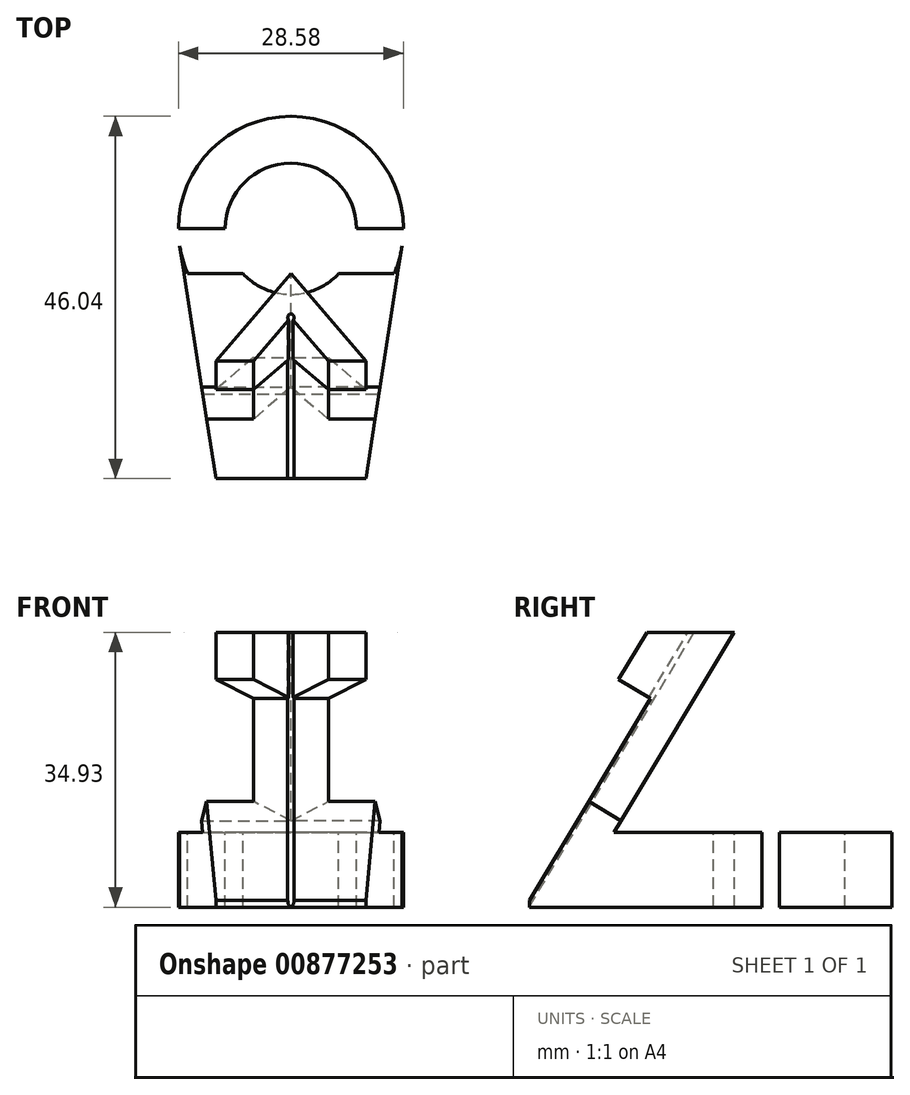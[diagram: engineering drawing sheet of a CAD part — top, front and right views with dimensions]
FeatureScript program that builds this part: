
annotation { "Feature Type Name" : "Feature", "Feature Type Description" : "" }
export const myFeature = defineFeature(function(context is Context, id is Id, definition is map)
    precondition{}
    {
        {
            var Q0;
            Q0=qCreatedBy(makeId("Top.planeOp"),FACE);
            var sketch = newSketch(context, id + "F0", { "sketchPlane" : qUnion([Q0])});
            skCircle(sketch, "E0", {"center": v(0, 0) * mm, "radius": 8.34 * mm});
            skCircle(sketch, "E1", {"center": v(0, 0) * mm, "radius": 14.29 * mm});
            skLineSegment(sketch, "E2", {"start": v(-14.12, -2.2) * mm, "end": v(-9.53, -31.75) * mm});
            skLineSegment(sketch, "E3", {"start": v(-9.53, -31.75) * mm, "end": v(0, -31.75) * mm});
            skLineSegment(sketch, "E4", {"start": v(0, 0) * mm, "end": v(0, -31.75) * mm, "construction": true});
            skLineSegment(sketch, "E5.MirrorCS", {"start": v(14.12, -2.2) * mm, "end": v(9.53, -31.75) * mm});
            skLineSegment(sketch, "E6.MirrorCS", {"start": v(9.53, -31.75) * mm, "end": v(0, -31.75) * mm});
            skLineSegment(sketch, "E7", {"start": v(0, -14.29) * mm, "end": v(-12.24, -14.29) * mm});
            skLineSegment(sketch, "E8.MirrorCS", {"start": v(0, -14.29) * mm, "end": v(12.24, -14.29) * mm});
            skCircle(sketch, "E9", {"center": v(0, 0) * mm, "radius": 5.72 * mm});
            skLineSegment(sketch, "E10", {"start": v(-14.29, 0) * mm, "end": v(14.29, 0) * mm});
            skLineSegment(sketch, "E11", {"start": v(0, -5.72) * mm, "end": v(-13.57, -5.72) * mm});
            skLineSegment(sketch, "E12.MirrorCS", {"start": v(0, -5.72) * mm, "end": v(13.57, -5.72) * mm});
            skSolve(sketch);
        }
        {
            var Q0;
            Q0=makeQuery(id+"F0.imprint","IMPRINT",FACE,{"disambiguationData":[TD([[makeQuery(id+"F0.imprint","IMPRINT",EDGE,{"derivedFrom":sQuery(id+"F0.wireOp",EDGE,"E0")}),-1.0]])]});
            var Q1;
            {var subQ3=sQuery(id+"F0.wireOp",EDGE,"E7");Q1=makeQuery(id+"F0.imprint","IMPRINT",FACE,{"disambiguationData":[TD([[makeQuery(id+"F0.imprint","IMPRINT",EDGE,{"derivedFrom":subQ3}),-1.0]])]});}
            var Q2;
            {var subQ3=sQuery(id+"F0.wireOp",EDGE,"E8.MirrorCS");Q2=makeQuery(id+"F0.imprint","IMPRINT",FACE,{"disambiguationData":[TD([[makeQuery(id+"F0.imprint","IMPRINT",EDGE,{"derivedFrom":subQ3}),1.0]])]});}
            var Q3;
            {var subQ3=sQuery(id+"F0.wireOp",EDGE,"E3");Q3=makeQuery(id+"F0.imprint","IMPRINT",FACE,{"disambiguationData":[TD([[makeQuery(id+"F0.imprint","IMPRINT",EDGE,{"derivedFrom":subQ3}),1.0]])]});}
            var Q4;
            {var subQ4=sQuery(id+"F0.wireOp",EDGE,"E10");var subQ6=sQuery(id+"F0.wireOp",EDGE,"E0");var subQ7=makeQuery(id+"F0.imprint","INTERSECT",VERTEX,{"disambiguationData":[OD(0.0)],"derivedFrom":[subQ6,subQ4]});Q4=makeQuery(id+"F0.imprint","IMPRINT",FACE,{"disambiguationData":[TD([[makeQuery(id+"F0.imprint","IMPRINT",EDGE,{"disambiguationData":[TD([[subQ7,-1.0]])],"derivedFrom":subQ6}),-1.0]])]});}
            var Q5;
            {var subQ2=sQuery(id+"F0.wireOp",EDGE,"E10");var subQ6=sQuery(id+"F0.wireOp",EDGE,"E0");var subQ7=makeQuery(id+"F0.imprint","INTERSECT",VERTEX,{"disambiguationData":[OD(1.0)],"derivedFrom":[subQ6,subQ2]});Q5=makeQuery(id+"F0.imprint","IMPRINT",FACE,{"disambiguationData":[TD([[makeQuery(id+"F0.imprint","IMPRINT",EDGE,{"disambiguationData":[TD([[subQ7,1.0]])],"derivedFrom":subQ6}),-1.0]])]});}
            var Q6;
            {var subQ0=sQuery(id+"F0.wireOp",EDGE,"E11");var subQ1=sQuery(id+"F0.wireOp",EDGE,"E0");var subQ2=makeQuery(id+"F0.imprint","INTERSECT",VERTEX,{"derivedFrom":[subQ1,subQ0]});Q6=makeQuery(id+"F0.imprint","IMPRINT",FACE,{"disambiguationData":[TD([[makeQuery(id+"F0.imprint","IMPRINT",EDGE,{"disambiguationData":[TD([[subQ2,-1.0]])],"derivedFrom":subQ1}),-1.0]])]});}
            var Q7;
            {var subQ0=sQuery(id+"F0.wireOp",EDGE,"E2");var subQ1=sQuery(id+"F0.wireOp",EDGE,"E1");var subQ2=makeQuery(id+"F0.imprint","INTERSECT",VERTEX,{"derivedFrom":[subQ1,subQ0]});Q7=makeQuery(id+"F0.imprint","IMPRINT",FACE,{"disambiguationData":[TD([[makeQuery(id+"F0.imprint","IMPRINT",EDGE,{"disambiguationData":[TD([[subQ2,-1.0]])],"derivedFrom":subQ1}),-1.0]])]});}
            var Q8;
            {var subQ0=sQuery(id+"F0.wireOp",EDGE,"E5.MirrorCS");var subQ1=sQuery(id+"F0.wireOp",EDGE,"E1");var subQ2=makeQuery(id+"F0.imprint","INTERSECT",VERTEX,{"derivedFrom":[subQ1,subQ0]});Q8=makeQuery(id+"F0.imprint","IMPRINT",FACE,{"disambiguationData":[TD([[makeQuery(id+"F0.imprint","IMPRINT",EDGE,{"disambiguationData":[TD([[subQ2,1.0]])],"derivedFrom":subQ1}),-1.0]])]});}
            extrude(context, id + "F1", {"entities" : qUnion([Q0, Q1, Q2, Q3, Q4, Q5, Q6, Q7, Q8]), "oppositeDirection" : true, "depth" : 9.52 * mm, "offsetDistance" : 25.4 * mm});
        }
        {
            var Q0;
            {var subQ3=sQuery(id+"F0.wireOp",EDGE,"E7");Q0=makeQuery(id+"F0.imprint","IMPRINT",FACE,{"disambiguationData":[TD([[makeQuery(id+"F0.imprint","IMPRINT",EDGE,{"derivedFrom":subQ3}),-1.0]])]});}
            var Q1;
            {var subQ3=sQuery(id+"F0.wireOp",EDGE,"E8.MirrorCS");Q1=makeQuery(id+"F0.imprint","IMPRINT",FACE,{"disambiguationData":[TD([[makeQuery(id+"F0.imprint","IMPRINT",EDGE,{"derivedFrom":subQ3}),1.0]])]});}
            var Q2;
            {var subQ3=sQuery(id+"F0.wireOp",EDGE,"E3");Q2=makeQuery(id+"F0.imprint","IMPRINT",FACE,{"disambiguationData":[TD([[makeQuery(id+"F0.imprint","IMPRINT",EDGE,{"derivedFrom":subQ3}),1.0]])]});}
            var Q3;
            {var subQ0=sQuery(id+"F0.wireOp",EDGE,"E11");var subQ1=sQuery(id+"F0.wireOp",EDGE,"E0");var subQ2=makeQuery(id+"F0.imprint","INTERSECT",VERTEX,{"derivedFrom":[subQ1,subQ0]});Q3=makeQuery(id+"F0.imprint","IMPRINT",FACE,{"disambiguationData":[TD([[makeQuery(id+"F0.imprint","IMPRINT",EDGE,{"disambiguationData":[TD([[subQ2,-1.0]])],"derivedFrom":subQ1}),-1.0]])]});}
            var Q4;
            {var subQ0=sQuery(id+"F0.wireOp",EDGE,"E11");var subQ1=sQuery(id+"F0.wireOp",EDGE,"E0");var subQ2=makeQuery(id+"F0.imprint","INTERSECT",VERTEX,{"derivedFrom":[subQ1,subQ0]});Q4=makeQuery(id+"F0.imprint","IMPRINT",FACE,{"disambiguationData":[TD([[makeQuery(id+"F0.imprint","IMPRINT",EDGE,{"disambiguationData":[TD([[subQ2,-1.0]])],"derivedFrom":subQ1}),1.0]])]});}
            extrude(context, id + "F2", {"entities" : qUnion([Q0, Q1, Q2, Q3, Q4]), "operationType" : NewBodyOperationType.ADD, "depth" : 25.4 * mm, "offsetDistance" : 25.4 * mm});
        }
        {
            var Q0;
            Q0=qCreatedBy(makeId("Right.planeOp"),FACE);
            cPlane(context, id + "F3", {"entities" : qUnion([Q0]), "cplaneType" : CPlaneType.OFFSET, "offset" : 14.29 * mm, "width" : 152.4 * mm, "height" : 152.4 * mm});
        }
        {
            var Q0;
            Q0=qCreatedBy(id+"F3.planeOp",FACE);
            var sketch = newSketch(context, id + "F4", { "sketchPlane" : qUnion([Q0])});
            skLineSegment(sketch, "E13", {"start": v(0, 0) * mm, "end": v(0, 25.4) * mm, "construction": true});
            skLineSegment(sketch, "E14", {"start": v(-5.72, 0) * mm, "end": v(-5.72, 25.4) * mm});
            skLineSegment(sketch, "E15", {"start": v(-5.71, 25.4) * mm, "end": v(-20.98, 0) * mm});
            skLineSegment(sketch, "E16", {"start": v(-16.83, 25.4) * mm, "end": v(-32.09, 0) * mm});
            skLineSegment(sketch, "E17", {"start": v(-11.27, 25.4) * mm, "end": v(-26.53, 0) * mm});
            skLineSegment(sketch, "E18", {"start": v(-12.26, 14.51) * mm, "end": v(-16.34, 16.97) * mm});
            skLineSegment(sketch, "E19", {"start": v(-32.09, 0) * mm, "end": v(-32.09, 25.4) * mm});
            skLineSegment(sketch, "E20", {"start": v(-32.09, 25.4) * mm, "end": v(-16.83, 25.4) * mm});
            skLineSegment(sketch, "E21", {"start": v(-20.98, 0) * mm, "end": v(-5.72, 0) * mm});
            skLineSegment(sketch, "E22", {"start": v(-16.34, 16.97) * mm, "end": v(-20.42, 19.42) * mm});
            skLineSegment(sketch, "E23", {"start": v(-26.53, 0) * mm, "end": v(-32.26, -9.53) * mm});
            skLineSegment(sketch, "E24", {"start": v(-32.26, -9.53) * mm, "end": v(-37.81, -9.53) * mm});
            skLineSegment(sketch, "E25", {"start": v(-32.09, 0) * mm, "end": v(-37.81, -9.53) * mm});
            skSolve(sketch);
        }
        {
            var Q0;
            Q0=makeQuery(id+"F4.imprint","IMPRINT",FACE,{"disambiguationData":[TD([[makeQuery(id+"F4.imprint","IMPRINT",EDGE,{"derivedFrom":sQuery(id+"F4.wireOp",EDGE,"E16")}),-1.0]])]});
            var Q1;
            {var subQ0=sQuery(id+"F4.wireOp",EDGE,"E14");Q1=makeQuery(id+"F4.imprint","IMPRINT",FACE,{"disambiguationData":[TD([[makeQuery(id+"F4.imprint","IMPRINT",EDGE,{"derivedFrom":subQ0}),1.0]])]});}
            var Q2;
            {var subQ2=sQuery(id+"F4.wireOp",EDGE,"E22");Q2=makeQuery(id+"F4.imprint","IMPRINT",FACE,{"disambiguationData":[TD([[makeQuery(id+"F4.imprint","IMPRINT",EDGE,{"derivedFrom":subQ2}),1.0]])]});}
            extrude(context, id + "F5", {"entities" : qUnion([Q0, Q1, Q2]), "operationType" : NewBodyOperationType.REMOVE, "endBound" : BoundingType.THROUGH_ALL, "oppositeDirection" : true, "depth" : 25.4 * mm, "offsetDistance" : 25.4 * mm});
        }
        {
            var Q0;
            Q0=makeQuery(id+"F5.boolean.opBoolean","MERGE",EDGE,{"derivedFrom":[makeQuery(id+"F2.opExtrude","CAP_EDGE",EDGE,{"disambiguationData":[OSD([sQuery(id+"F0.wireOp",EDGE,"E11"),sQuery(id+"F0.wireOp",EDGE,"E12.MirrorCS")])],"isStart":false})],"fromTools":[makeQuery(id+"F5.opExtrude","SWEPT_EDGE",EDGE,{"disambiguationData":[OSD([sQuery(id+"F4.wireOp",EDGE,"E14"),sQuery(id+"F4.wireOp",EDGE,"E15")])]})]});
            cPlane(context, id + "F6", {"entities" : qUnion([Q0]), "cplaneType" : CPlaneType.LINE_ANGLE, "offset" : 25.4 * mm, "angle" : 59 * degree, "oppositeDirection" : true, "width" : 152.4 * mm, "height" : 152.4 * mm});
        }
        {
            var Q0;
            Q0=qCreatedBy(id+"F6.planeOp",FACE);
            var sketch = newSketch(context, id + "F7", { "sketchPlane" : qUnion([Q0])});
            skLineSegment(sketch, "E26", {"start": v(0, 17.98) * mm, "end": v(9.52, 27.5) * mm});
            skLineSegment(sketch, "E27", {"start": v(0, 17.98) * mm, "end": v(0, 31.26) * mm, "construction": true});
            skLineSegment(sketch, "E28.MirrorCS", {"start": v(0, 17.98) * mm, "end": v(-9.52, 27.5) * mm});
            skLineSegment(sketch, "E29", {"start": v(14.02, 27.5) * mm, "end": v(4.5, 17.98) * mm});
            skLineSegment(sketch, "E30.MirrorCS", {"start": v(-14.02, 27.5) * mm, "end": v(-4.5, 17.98) * mm});
            skLineSegment(sketch, "E31", {"start": v(0, 22.74) * mm, "end": v(13.57, 22.74) * mm});
            skLineSegment(sketch, "E32.MirrorCS", {"start": v(0, 22.74) * mm, "end": v(-13.57, 22.74) * mm});
            skLineSegment(sketch, "E33", {"start": v(9.52, 27.5) * mm, "end": v(14.02, 27.5) * mm});
            skLineSegment(sketch, "E34", {"start": v(4.5, 17.98) * mm, "end": v(0, 17.98) * mm});
            skLineSegment(sketch, "E35", {"start": v(9.52, 27.5) * mm, "end": v(0, 27.5) * mm});
            skLineSegment(sketch, "E36.MirrorCS", {"start": v(-9.52, 27.5) * mm, "end": v(0, 27.5) * mm});
            skLineSegment(sketch, "E37.MirrorCS", {"start": v(-4.5, 17.98) * mm, "end": v(0, 17.98) * mm});
            skLineSegment(sketch, "E38.MirrorCS", {"start": v(-9.52, 27.5) * mm, "end": v(-14.02, 27.5) * mm});
            skLineSegment(sketch, "E39", {"start": v(0, 22.74) * mm, "end": v(4.76, 27.5) * mm});
            skLineSegment(sketch, "E40.MirrorCS", {"start": v(0, 22.74) * mm, "end": v(-4.76, 27.5) * mm});
            skCircle(sketch, "E41", {"center": v(0, 22.74) * mm, "radius": 0.4 * mm});
            skLineSegment(sketch, "E42", {"start": v(13.57, 22.74) * mm, "end": v(13.57, 17.98) * mm});
            skLineSegment(sketch, "E43", {"start": v(13.57, 17.98) * mm, "end": v(4.5, 17.98) * mm});
            skLineSegment(sketch, "E44.MirrorCS", {"start": v(-13.57, 17.98) * mm, "end": v(-4.5, 17.98) * mm});
            skLineSegment(sketch, "E45.MirrorCS", {"start": v(-13.57, 22.74) * mm, "end": v(-13.57, 17.98) * mm});
            skLineSegment(sketch, "E46", {"start": v(13.57, 22.74) * mm, "end": v(13.57, 27.06) * mm});
            skLineSegment(sketch, "E47.MirrorCS", {"start": v(-13.57, 22.74) * mm, "end": v(-13.57, 27.06) * mm});
            skSolve(sketch);
        }
        {
            var Q0;
            {var subQ1=sQuery(id+"F7.wireOp",EDGE,"E36.MirrorCS");var subQ6=sQuery(id+"F7.wireOp",EDGE,"E35");var subQ9=makeQuery(id+"F7.imprint","INTERSECT",VERTEX,{"derivedFrom":[subQ6,subQ1]});Q0=makeQuery(id+"F7.imprint","IMPRINT",FACE,{"disambiguationData":[TD([[makeQuery(id+"F7.imprint","IMPRINT",EDGE,{"disambiguationData":[TD([[subQ9,1.0]])],"derivedFrom":subQ6}),1.0]])]});}
            var Q1;
            {var subQ1=sQuery(id+"F7.wireOp",EDGE,"E32.MirrorCS");var subQ3=sQuery(id+"F7.wireOp",EDGE,"E41");var subQ4=makeQuery(id+"F7.imprint","INTERSECT",VERTEX,{"derivedFrom":[subQ1,subQ3]});Q1=makeQuery(id+"F7.imprint","IMPRINT",FACE,{"disambiguationData":[TD([[makeQuery(id+"F7.imprint","IMPRINT",EDGE,{"disambiguationData":[TD([[subQ4,1.0]])],"derivedFrom":subQ3}),1.0]])]});}
            var Q2;
            {var subQ1=sQuery(id+"F7.wireOp",EDGE,"E31");var subQ3=sQuery(id+"F7.wireOp",EDGE,"E41");var subQ4=makeQuery(id+"F7.imprint","INTERSECT",VERTEX,{"derivedFrom":[subQ1,subQ3]});Q2=makeQuery(id+"F7.imprint","IMPRINT",FACE,{"disambiguationData":[TD([[makeQuery(id+"F7.imprint","IMPRINT",EDGE,{"disambiguationData":[TD([[subQ4,-1.0]])],"derivedFrom":subQ3}),1.0]])]});}
            var Q3;
            {var subQ1=sQuery(id+"F7.wireOp",EDGE,"E39");var subQ3=sQuery(id+"F7.wireOp",EDGE,"E41");var subQ4=makeQuery(id+"F7.imprint","INTERSECT",VERTEX,{"derivedFrom":[subQ1,subQ3]});Q3=makeQuery(id+"F7.imprint","IMPRINT",FACE,{"disambiguationData":[TD([[makeQuery(id+"F7.imprint","IMPRINT",EDGE,{"disambiguationData":[TD([[subQ4,-1.0]])],"derivedFrom":subQ3}),1.0]])]});}
            var Q4;
            {var subQ1=sQuery(id+"F7.wireOp",EDGE,"E31");var subQ3=sQuery(id+"F7.wireOp",EDGE,"E41");var subQ4=makeQuery(id+"F7.imprint","INTERSECT",VERTEX,{"derivedFrom":[subQ1,subQ3]});Q4=makeQuery(id+"F7.imprint","IMPRINT",FACE,{"disambiguationData":[TD([[makeQuery(id+"F7.imprint","IMPRINT",EDGE,{"disambiguationData":[TD([[subQ4,1.0]])],"derivedFrom":subQ3}),1.0]])]});}
            extrude(context, id + "F8", {"entities" : qUnion([Q0, Q1, Q2, Q3, Q4]), "operationType" : NewBodyOperationType.REMOVE, "endBound" : BoundingType.THROUGH_ALL, "depth" : 25.4 * mm, "offsetDistance" : 25.4 * mm});
        }
        {
            var Q0;
            {var subQ0=sQuery(id+"F7.wireOp",EDGE,"E33");Q0=makeQuery(id+"F7.imprint","IMPRINT",FACE,{"disambiguationData":[TD([[makeQuery(id+"F7.imprint","IMPRINT",EDGE,{"derivedFrom":subQ0}),-1.0]])]});}
            var Q1;
            {var subQ4=sQuery(id+"F7.wireOp",EDGE,"E42");Q1=makeQuery(id+"F7.imprint","IMPRINT",FACE,{"disambiguationData":[TD([[makeQuery(id+"F7.imprint","IMPRINT",EDGE,{"derivedFrom":subQ4}),-1.0]])]});}
            var Q2;
            {var subQ0=sQuery(id+"F7.wireOp",EDGE,"E44.MirrorCS");Q2=makeQuery(id+"F7.imprint","IMPRINT",FACE,{"disambiguationData":[TD([[makeQuery(id+"F7.imprint","IMPRINT",EDGE,{"derivedFrom":subQ0}),1.0]])]});}
            var Q3;
            {var subQ0=sQuery(id+"F7.wireOp",EDGE,"E46");Q3=makeQuery(id+"F7.imprint","IMPRINT",FACE,{"disambiguationData":[TD([[makeQuery(id+"F7.imprint","IMPRINT",EDGE,{"derivedFrom":subQ0}),1.0]])]});}
            var Q4;
            {var subQ5=sQuery(id+"F7.wireOp",EDGE,"E38.MirrorCS");Q4=makeQuery(id+"F7.imprint","IMPRINT",FACE,{"disambiguationData":[TD([[makeQuery(id+"F7.imprint","IMPRINT",EDGE,{"derivedFrom":subQ5}),1.0]])]});}
            var Q5;
            {var subQ0=sQuery(id+"F7.wireOp",EDGE,"E47.MirrorCS");Q5=makeQuery(id+"F7.imprint","IMPRINT",FACE,{"disambiguationData":[TD([[makeQuery(id+"F7.imprint","IMPRINT",EDGE,{"derivedFrom":subQ0}),-1.0]])]});}
            var Q6;
            {var subQ0=sQuery(id+"F7.wireOp",EDGE,"E34");Q6=makeQuery(id+"F7.imprint","IMPRINT",FACE,{"disambiguationData":[TD([[makeQuery(id+"F7.imprint","IMPRINT",EDGE,{"derivedFrom":subQ0}),-1.0]])]});}
            var Q7;
            {var subQ0=sQuery(id+"F7.wireOp",EDGE,"E37.MirrorCS");Q7=makeQuery(id+"F7.imprint","IMPRINT",FACE,{"disambiguationData":[TD([[makeQuery(id+"F7.imprint","IMPRINT",EDGE,{"derivedFrom":subQ0}),1.0]])]});}
            extrude(context, id + "F9", {"entities" : qUnion([Q0, Q1, Q2, Q3, Q4, Q5, Q6, Q7]), "operationType" : NewBodyOperationType.REMOVE, "depth" : 27.94 * mm, "offsetDistance" : 25.4 * mm});
        }
    });
